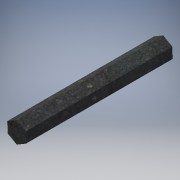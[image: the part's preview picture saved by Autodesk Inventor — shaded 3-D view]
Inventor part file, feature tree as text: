
AUTODESK INVENTOR PART (.ipt)
format: ipt  version: 2016 (Build 200138000, 138)  size: 102,912 bytes
history: native  units: in
note: dims shown in document units (in); Inventor stores cm internally (conversion verified against a paired STEP export)
features: extrude x1, sketch x1
ambient origin geometry x8: Origin, YZ Plane, XZ Plane, XY Plane, X Axis, Y Axis, Z Axis, Center Point
bodies: Solid1 (feature_tree)
feature tree (2):
  extrude  "Extrusion1"  Depth=4.0in TaperAngle=0.0deg
  sketch  "Sketch1"  dims[d0=0.5in d1=4.0in d2=0.0in]
